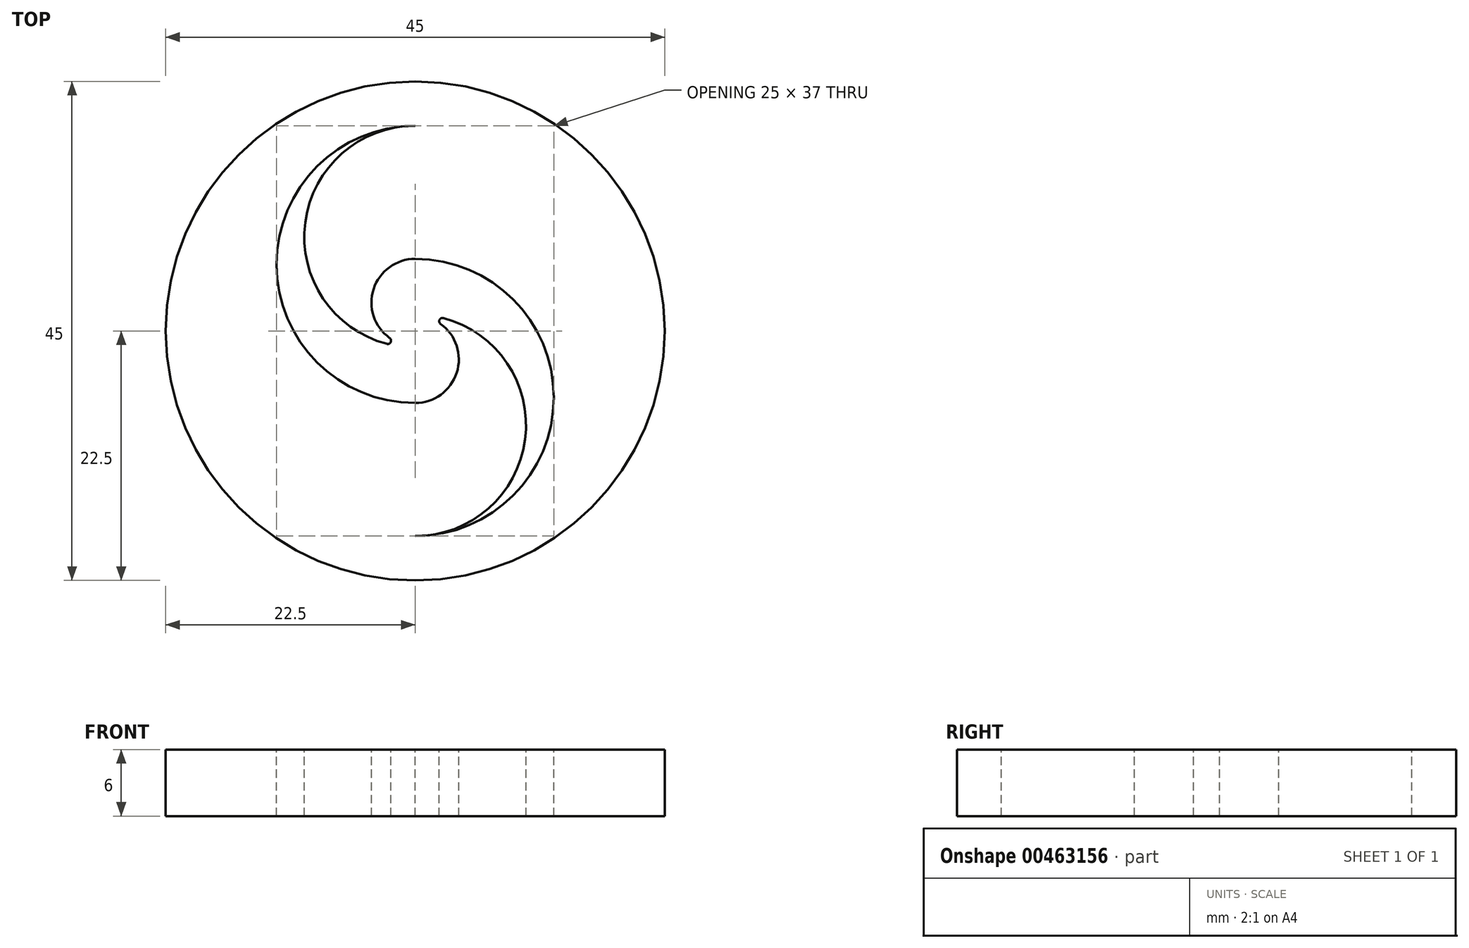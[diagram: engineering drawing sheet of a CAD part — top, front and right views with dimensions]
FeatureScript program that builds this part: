
annotation { "Feature Type Name" : "Feature", "Feature Type Description" : "" }
export const myFeature = defineFeature(function(context is Context, id is Id, definition is map)
    precondition{}
    {
        {
            var Q0;
            Q0=qCreatedBy(makeId("Top.planeOp"),FACE);
            var sketch = newSketch(context, id + "F0", { "sketchPlane" : qUnion([Q0])});
            skCircle(sketch, "E0", {"center": v(0, 0) * mm, "radius": 22.5 * mm});
            skSolve(sketch);
        }
        {
            var Q0;
            Q0 = qSketchRegion(id + "F0", true);
            extrude(context, id + "F1", {"entities" : qUnion([Q0]), "depth" : 6 * mm});
        }
        {
            var Q0;
            Q0=makeQuery(id+"F1.opExtrude","CAP_FACE",FACE,{"disambiguationData":[OSD([sQuery(id+"F0.wireOp",EDGE,"E0")])],"isStart":false});
            var sketch = newSketch(context, id + "F2", { "sketchPlane" : qUnion([Q0])});
            skCircle(sketch, "E1", {"center": v(0, 0) * mm, "radius": 18.5 * mm, "construction": true});
            skArc(sketch, "E2", {"start": v(0, -6.5) * mm, "mid": v(2.5, -4) * mm, "end": v(0, -1.5) * mm});
            skCircle(sketch, "E3", {"center": v(0, 0) * mm, "radius": 1.5 * mm, "construction": true});
            skArc(sketch, "E4", {"start": v(0, 18.5) * mm, "mid": v(-10, 8.5) * mm, "end": v(0, -1.5) * mm});
            skArc(sketch, "E5", {"start": v(0, 18.5) * mm, "mid": v(-12.5, 6) * mm, "end": v(0, -6.5) * mm});
            skPoint(sketch, "E6", {"position": v(0, 18.5) * mm});
            skArc(sketch, "E7.1.0", {"start": v(0, -18.5) * mm, "mid": v(10, -8.5) * mm, "end": v(0, 1.5) * mm});
            skArc(sketch, "E7.1.1", {"start": v(0, 6.5) * mm, "mid": v(-2.5, 4) * mm, "end": v(0, 1.5) * mm});
            skArc(sketch, "E7.1.2", {"start": v(0, -18.5) * mm, "mid": v(12.5, -6) * mm, "end": v(0, 6.5) * mm});
            skSolve(sketch);
        }
        {
            var Q0;
            Q0 = qSketchRegion(id + "F2", true);
            extrude(context, id + "F3", {"entities" : qUnion([Q0]), "operationType" : NewBodyOperationType.REMOVE, "oppositeDirection" : true, "depth" : 25 * mm});
        }
        {
            var Q0;
            Q0=makeQuery(id+"F1.opExtrude","CAP_FACE",FACE,{"disambiguationData":[OSD([sQuery(id+"F0.wireOp",EDGE,"E0")])],"isStart":false});
            var sketch = newSketch(context, id + "F4", { "sketchPlane" : qUnion([Q0])});
            skArc(sketch, "E8", {"start": v(2.55, 1.17) * mm, "mid": v(2.2, 1) * mm, "end": v(2.3, 0.64) * mm});
            skArc(sketch, "E9", {"start": v(0, -6.5) * mm, "mid": v(3.75, -3.77) * mm, "end": v(2.3, 0.64) * mm});
            skArc(sketch, "E10", {"start": v(2.55, 1.17) * mm, "mid": v(1.29, 1.42) * mm, "end": v(0, 1.5) * mm});
            skArc(sketch, "E11", {"start": v(0, -1.5) * mm, "mid": v(-2.5, -4) * mm, "end": v(0, -6.5) * mm});
            skLineSegment(sketch, "E12", {"start": v(0, 1.5) * mm, "end": v(0, -1.5) * mm});
            skArc(sketch, "E13.1.0", {"start": v(0, 1.5) * mm, "mid": v(2.5, 4) * mm, "end": v(0, 6.5) * mm});
            skArc(sketch, "E13.1.1", {"start": v(0, 6.5) * mm, "mid": v(-3.75, 3.77) * mm, "end": v(-2.3, -0.64) * mm});
            skArc(sketch, "E13.1.2", {"start": v(-2.55, -1.17) * mm, "mid": v(-2.2, -1) * mm, "end": v(-2.3, -0.64) * mm});
            skArc(sketch, "E13.1.3", {"start": v(-2.55, -1.17) * mm, "mid": v(-1.29, -1.42) * mm, "end": v(0, -1.5) * mm});
            skLineSegment(sketch, "E13.1.4", {"start": v(0, -1.5) * mm, "end": v(0, 1.5) * mm});
            skPoint(sketch, "E13.center", {"position": v(0, 0) * mm});
            skSolve(sketch);
        }
        {
            var Q0;
            Q0 = qSketchRegion(id + "F4", true);
            extrude(context, id + "F5", {"entities" : qUnion([Q0]), "operationType" : NewBodyOperationType.REMOVE, "oppositeDirection" : true, "depth" : 25 * mm});
        }
    });
